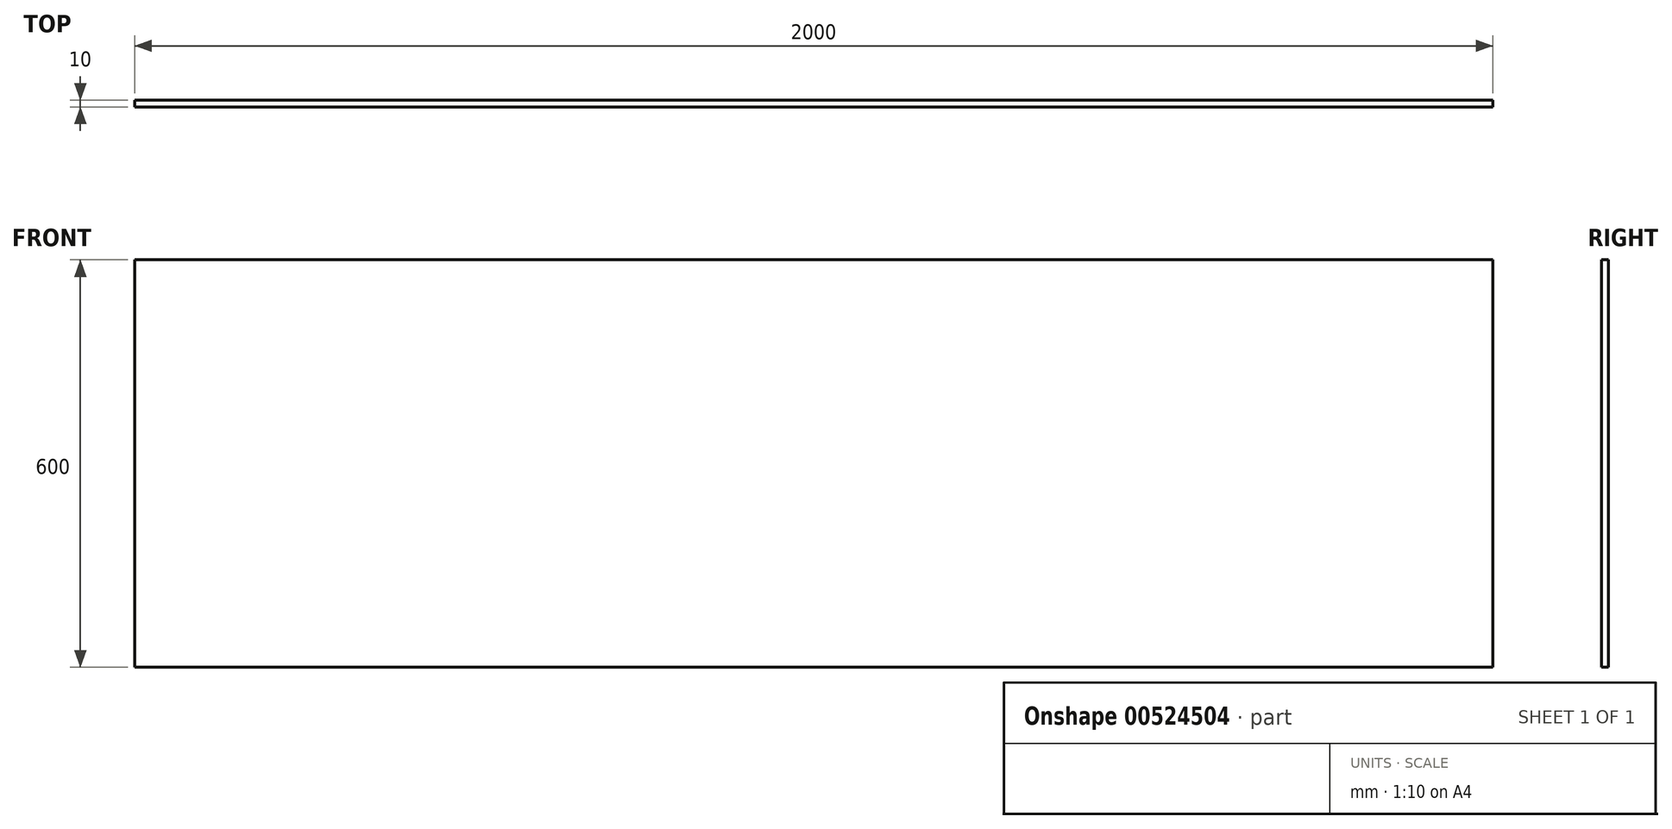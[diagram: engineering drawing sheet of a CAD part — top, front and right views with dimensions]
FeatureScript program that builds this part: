
annotation { "Feature Type Name" : "Feature", "Feature Type Description" : "" }
export const myFeature = defineFeature(function(context is Context, id is Id, definition is map)
    precondition{}
    {
        {
            var Q0;
            Q0=qCreatedBy(makeId("Front.planeOp"),FACE);
            var sketch = newSketch(context, id + "F0", { "sketchPlane" : qUnion([Q0])});
            skLineSegment(sketch, "E0.bottom", {"start": v(-1000, -323.24) * mm, "end": v(1000, -323.24) * mm});
            skLineSegment(sketch, "E0.top", {"start": v(-1000, 276.76) * mm, "end": v(1000, 276.76) * mm});
            skLineSegment(sketch, "E0.left", {"start": v(-1000, -323.24) * mm, "end": v(-1000, 276.76) * mm});
            skLineSegment(sketch, "E0.right", {"start": v(1000, -323.24) * mm, "end": v(1000, 276.76) * mm});
            skPoint(sketch, "E0.middle", {"position": v(0, -23.24) * mm});
            skSolve(sketch);
        }
        {
            var Q0;
            Q0=makeQuery(id+"F0.imprint","IMPRINT",FACE,{"disambiguationData":[TD([[makeQuery(id+"F0.imprint","IMPRINT",EDGE,{"derivedFrom":sQuery(id+"F0.wireOp",EDGE,"E0.bottom")}),1.0]])]});
            extrude(context, id + "F1", {"entities" : qUnion([Q0]), "depth" : 10 * mm, "offsetDistance" : 25 * mm});
        }
    });
